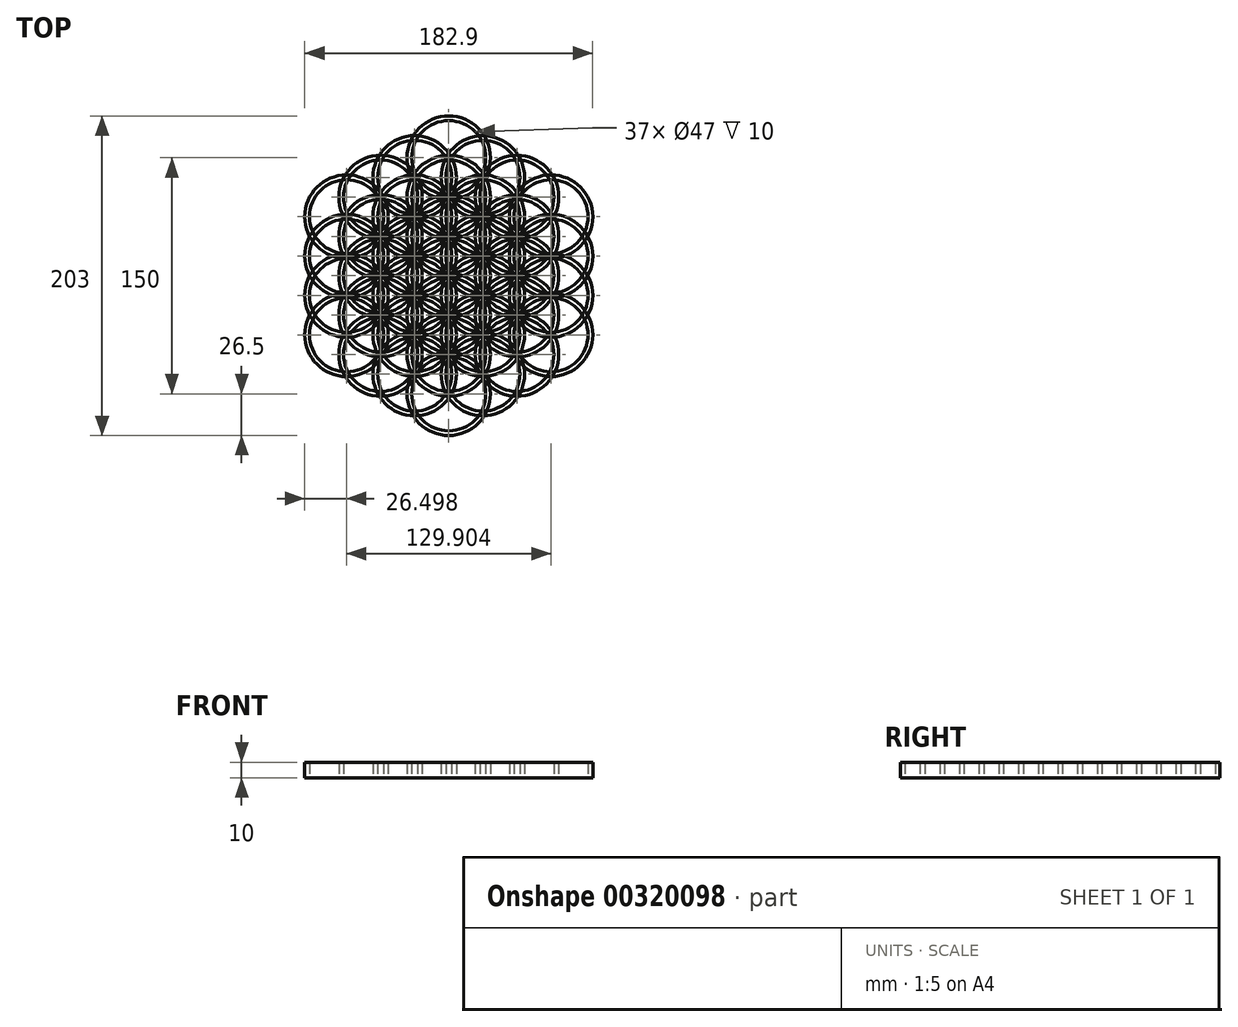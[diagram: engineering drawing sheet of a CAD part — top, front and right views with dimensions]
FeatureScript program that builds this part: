
annotation { "Feature Type Name" : "Feature", "Feature Type Description" : "" }
export const myFeature = defineFeature(function(context is Context, id is Id, definition is map)
    precondition{}
    {
        {
            var Q0;
            Q0=qCreatedBy(makeId("Right.planeOp"),FACE);
            var sketch = newSketch(context, id + "F0", { "sketchPlane" : qUnion([Q0])});
            skLineSegment(sketch, "E0", {"start": v(0, 0) * mm, "end": v(0, -9.37) * mm});
            skSolve(sketch);
        }
        {
            var Q0;
            Q0=qCreatedBy(makeId("Top.planeOp"),FACE);
            var sketch = newSketch(context, id + "F1", { "sketchPlane" : qUnion([Q0])});
            skCircle(sketch, "E1", {"center": v(0, 0) * mm, "radius": 25 * mm, "construction": true});
            skCircle(sketch, "E2.0", {"center": v(0, 0) * mm, "radius": 26.5 * mm});
            skCircle(sketch, "E3.0", {"center": v(0, 0) * mm, "radius": 23.5 * mm});
            skSolve(sketch);
        }
        {
            var Q0;
            Q0=makeQuery(id+"F1.imprint","IMPRINT",FACE,{"disambiguationData":[TD([[makeQuery(id+"F1.imprint","IMPRINT",EDGE,{"derivedFrom":sQuery(id+"F1.wireOp",EDGE,"E2.0")}),1.0]])]});
            extrude(context, id + "F2", {"entities" : qUnion([Q0]), "depth" : 10 * mm});
        }
        {
            var Q0;
            Q0=qCreatedBy(makeId("Top.planeOp"),FACE);
            var sketch = newSketch(context, id + "F3", { "sketchPlane" : qUnion([Q0])});
            skCircle(sketch, "E4", {"center": v(0, 25) * mm, "radius": 25 * mm, "construction": true});
            skCircle(sketch, "E5.0", {"center": v(0, 25) * mm, "radius": 26.5 * mm});
            skCircle(sketch, "E6.0", {"center": v(0, 25) * mm, "radius": 23.5 * mm});
            skCircle(sketch, "E7", {"center": v(0, 0) * mm, "radius": 25 * mm, "construction": true});
            skCircle(sketch, "E8.0", {"center": v(0, 0) * mm, "radius": 26.5 * mm, "construction": true});
            skCircle(sketch, "E9.0", {"center": v(0, 0) * mm, "radius": 23.5 * mm, "construction": true});
            skSolve(sketch);
        }
        {
            var Q0;
            Q0 = qSketchRegion(id + "F3", true);
            extrude(context, id + "F4", {"entities" : qUnion([Q0]), "depth" : 10 * mm});
        }
        {
            var Q0;
            Q0=makeQuery(id+"F4.opExtrude","SWEPT_BODY",BODY,{"disambiguationData":[OSD([sQuery(id+"F3.wireOp",EDGE,"E5.0"),sQuery(id+"F3.wireOp",EDGE,"E6.0")])]});
            var Q1;
            Q1=sQuery(id+"F0.wireOp",EDGE,"E0");
            circularPattern(context, id + "F5", {"entities" : qUnion([Q0]), "axis" : qUnion([Q1]), "angle" : 360 * degree, "instanceCount" : 6, "equalSpace" : true});
        }
        {
            var Q0;
            Q0=qCreatedBy(makeId("Top.planeOp"),FACE);
            var sketch = newSketch(context, id + "F6", { "sketchPlane" : qUnion([Q0])});
            skCircle(sketch, "E10", {"center": v(0, 0) * mm, "radius": 25 * mm, "construction": true});
            skCircle(sketch, "E11.0", {"center": v(0, 0) * mm, "radius": 26.5 * mm, "construction": true});
            skCircle(sketch, "E12.0", {"center": v(0, 0) * mm, "radius": 23.5 * mm, "construction": true});
            skCircle(sketch, "E13", {"center": v(0, 25) * mm, "radius": 25 * mm, "construction": true});
            skCircle(sketch, "E14.0", {"center": v(0, 25) * mm, "radius": 26.5 * mm, "construction": true});
            skCircle(sketch, "E15.0", {"center": v(0, 25) * mm, "radius": 23.5 * mm, "construction": true});
            skCircle(sketch, "E16", {"center": v(-21.65, 12.5) * mm, "radius": 25 * mm, "construction": true});
            skCircle(sketch, "E17.0", {"center": v(-21.65, 12.5) * mm, "radius": 26.5 * mm, "construction": true});
            skCircle(sketch, "E18.0", {"center": v(-21.65, 12.5) * mm, "radius": 23.5 * mm, "construction": true});
            skCircle(sketch, "E19", {"center": v(-21.65, 37.5) * mm, "radius": 25 * mm, "construction": true});
            skCircle(sketch, "E20.0", {"center": v(-21.65, 37.5) * mm, "radius": 26.5 * mm});
            skCircle(sketch, "E21.0", {"center": v(-21.65, 37.5) * mm, "radius": 23.5 * mm});
            skSolve(sketch);
        }
        {
            var Q0;
            Q0=makeQuery(id+"F6.imprint","IMPRINT",FACE,{"disambiguationData":[TD([[makeQuery(id+"F6.imprint","IMPRINT",EDGE,{"derivedFrom":sQuery(id+"F6.wireOp",EDGE,"E20.0")}),1.0]])]});
            extrude(context, id + "F7", {"entities" : qUnion([Q0]), "depth" : 10 * mm});
        }
        {
            var Q0;
            Q0=makeQuery(id+"F7.opExtrude","SWEPT_BODY",BODY,{"disambiguationData":[OSD([sQuery(id+"F6.wireOp",EDGE,"E20.0"),sQuery(id+"F6.wireOp",EDGE,"E21.0")])]});
            var Q1;
            Q1=sQuery(id+"F0.wireOp",EDGE,"E0");
            circularPattern(context, id + "F8", {"entities" : qUnion([Q0]), "axis" : qUnion([Q1]), "angle" : 360 * degree, "instanceCount" : 6, "equalSpace" : true});
        }
        {
            var Q0;
            Q0=qCreatedBy(makeId("Top.planeOp"),FACE);
            var sketch = newSketch(context, id + "F9", { "sketchPlane" : qUnion([Q0])});
            skCircle(sketch, "E22", {"center": v(0, 0) * mm, "radius": 25 * mm, "construction": true});
            skCircle(sketch, "E23.0", {"center": v(0, 0) * mm, "radius": 26.5 * mm, "construction": true});
            skCircle(sketch, "E24.0", {"center": v(0, 0) * mm, "radius": 23.5 * mm, "construction": true});
            skCircle(sketch, "E25", {"center": v(0, 25) * mm, "radius": 25 * mm, "construction": true});
            skCircle(sketch, "E26.0", {"center": v(0, 25) * mm, "radius": 26.5 * mm, "construction": true});
            skCircle(sketch, "E27.0", {"center": v(0, 25) * mm, "radius": 23.5 * mm, "construction": true});
            skCircle(sketch, "E28", {"center": v(-21.65, 12.5) * mm, "radius": 25 * mm, "construction": true});
            skCircle(sketch, "E29.0", {"center": v(-21.65, 12.5) * mm, "radius": 26.5 * mm, "construction": true});
            skCircle(sketch, "E30.0", {"center": v(-21.65, 12.5) * mm, "radius": 23.5 * mm, "construction": true});
            skCircle(sketch, "E31", {"center": v(-21.65, 37.5) * mm, "radius": 25 * mm, "construction": true});
            skCircle(sketch, "E32.0", {"center": v(-21.65, 37.5) * mm, "radius": 26.5 * mm, "construction": true});
            skCircle(sketch, "E33.0", {"center": v(-21.65, 37.5) * mm, "radius": 23.5 * mm, "construction": true});
            skCircle(sketch, "E34", {"center": v(-80.96, 35.25) * mm, "radius": 20 * mm, "construction": true});
            skCircle(sketch, "E35.0", {"center": v(-80.96, 35.25) * mm, "radius": 21.5 * mm, "construction": true});
            skCircle(sketch, "E36.0", {"center": v(-80.96, 35.25) * mm, "radius": 18.5 * mm, "construction": true});
            skCircle(sketch, "E37", {"center": v(-43.3, 25) * mm, "radius": 25 * mm, "construction": true});
            skCircle(sketch, "E38.0", {"center": v(-43.3, 25) * mm, "radius": 26.5 * mm});
            skCircle(sketch, "E39.0", {"center": v(-43.3, 25) * mm, "radius": 23.5 * mm});
            skSolve(sketch);
        }
        {
            var Q0;
            Q0=makeQuery(id+"F9.imprint","IMPRINT",FACE,{"disambiguationData":[TD([[makeQuery(id+"F9.imprint","IMPRINT",EDGE,{"derivedFrom":sQuery(id+"F9.wireOp",EDGE,"E38.0")}),1.0]])]});
            extrude(context, id + "F10", {"entities" : qUnion([Q0]), "depth" : 10 * mm});
        }
        {
            var Q0;
            Q0=makeQuery(id+"F10.opExtrude","SWEPT_BODY",BODY,{"disambiguationData":[OSD([sQuery(id+"F9.wireOp",EDGE,"E38.0"),sQuery(id+"F9.wireOp",EDGE,"E39.0")])]});
            var Q1;
            Q1=sQuery(id+"F0.wireOp",EDGE,"E0");
            circularPattern(context, id + "F11", {"entities" : qUnion([Q0]), "axis" : qUnion([Q1]), "angle" : 360 * degree, "instanceCount" : 6, "equalSpace" : true});
        }
        {
            var Q0;
            Q0=qCreatedBy(makeId("Top.planeOp"),FACE);
            var sketch = newSketch(context, id + "F12", { "sketchPlane" : qUnion([Q0])});
            skCircle(sketch, "E40", {"center": v(0, 0) * mm, "radius": 25 * mm, "construction": true});
            skCircle(sketch, "E41.0", {"center": v(0, 0) * mm, "radius": 26.5 * mm, "construction": true});
            skCircle(sketch, "E42.0", {"center": v(0, 0) * mm, "radius": 23.5 * mm, "construction": true});
            skCircle(sketch, "E43", {"center": v(0, 25) * mm, "radius": 25 * mm, "construction": true});
            skCircle(sketch, "E44.0", {"center": v(0, 25) * mm, "radius": 26.5 * mm, "construction": true});
            skCircle(sketch, "E45.0", {"center": v(0, 25) * mm, "radius": 23.5 * mm, "construction": true});
            skCircle(sketch, "E46", {"center": v(-21.65, 12.5) * mm, "radius": 25 * mm, "construction": true});
            skCircle(sketch, "E47.0", {"center": v(-21.65, 12.5) * mm, "radius": 26.5 * mm, "construction": true});
            skCircle(sketch, "E48.0", {"center": v(-21.65, 12.5) * mm, "radius": 23.5 * mm, "construction": true});
            skCircle(sketch, "E49", {"center": v(-21.65, 37.5) * mm, "radius": 25 * mm, "construction": true});
            skCircle(sketch, "E50.0", {"center": v(-21.65, 37.5) * mm, "radius": 26.5 * mm, "construction": true});
            skCircle(sketch, "E51.0", {"center": v(-21.65, 37.5) * mm, "radius": 23.5 * mm, "construction": true});
            skCircle(sketch, "E52", {"center": v(-43.3, 50) * mm, "radius": 25 * mm, "construction": true});
            skCircle(sketch, "E53.0", {"center": v(-43.3, 50) * mm, "radius": 26.5 * mm});
            skCircle(sketch, "E54.0", {"center": v(-43.3, 50) * mm, "radius": 23.5 * mm});
            skCircle(sketch, "E55", {"center": v(-43.3, 25) * mm, "radius": 25 * mm, "construction": true});
            skCircle(sketch, "E56.0", {"center": v(-43.3, 25) * mm, "radius": 26.5 * mm, "construction": true});
            skCircle(sketch, "E57.0", {"center": v(-43.3, 25) * mm, "radius": 23.5 * mm, "construction": true});
            skSolve(sketch);
        }
        {
            var Q0;
            Q0=makeQuery(id+"F12.imprint","IMPRINT",FACE,{"disambiguationData":[TD([[makeQuery(id+"F12.imprint","IMPRINT",EDGE,{"derivedFrom":sQuery(id+"F12.wireOp",EDGE,"E53.0")}),1.0]])]});
            extrude(context, id + "F13", {"entities" : qUnion([Q0]), "depth" : 10 * mm});
        }
        {
            var Q0;
            Q0=makeQuery(id+"F13.opExtrude","SWEPT_BODY",BODY,{"disambiguationData":[OSD([sQuery(id+"F12.wireOp",EDGE,"E53.0"),sQuery(id+"F12.wireOp",EDGE,"E54.0")])]});
            var Q1;
            Q1=sQuery(id+"F0.wireOp",EDGE,"E0");
            circularPattern(context, id + "F14", {"entities" : qUnion([Q0]), "axis" : qUnion([Q1]), "angle" : 360 * degree, "instanceCount" : 6, "equalSpace" : true});
        }
        {
            var Q0;
            Q0=qCreatedBy(makeId("Top.planeOp"),FACE);
            var sketch = newSketch(context, id + "F15", { "sketchPlane" : qUnion([Q0])});
            skCircle(sketch, "E58", {"center": v(0, 0) * mm, "radius": 25 * mm, "construction": true});
            skCircle(sketch, "E59.0", {"center": v(0, 0) * mm, "radius": 26.5 * mm, "construction": true});
            skCircle(sketch, "E60.0", {"center": v(0, 0) * mm, "radius": 23.5 * mm, "construction": true});
            skCircle(sketch, "E61", {"center": v(0, 25) * mm, "radius": 25 * mm, "construction": true});
            skCircle(sketch, "E62.0", {"center": v(0, 25) * mm, "radius": 26.5 * mm, "construction": true});
            skCircle(sketch, "E63.0", {"center": v(0, 25) * mm, "radius": 23.5 * mm, "construction": true});
            skCircle(sketch, "E64", {"center": v(-21.65, 12.5) * mm, "radius": 25 * mm, "construction": true});
            skCircle(sketch, "E65.0", {"center": v(-21.65, 12.5) * mm, "radius": 26.5 * mm, "construction": true});
            skCircle(sketch, "E66.0", {"center": v(-21.65, 12.5) * mm, "radius": 23.5 * mm, "construction": true});
            skCircle(sketch, "E67", {"center": v(-21.65, 37.5) * mm, "radius": 25 * mm, "construction": true});
            skCircle(sketch, "E68.0", {"center": v(-21.65, 37.5) * mm, "radius": 26.5 * mm, "construction": true});
            skCircle(sketch, "E69.0", {"center": v(-21.65, 37.5) * mm, "radius": 23.5 * mm, "construction": true});
            skCircle(sketch, "E70", {"center": v(-43.3, 50) * mm, "radius": 25 * mm, "construction": true});
            skCircle(sketch, "E71.0", {"center": v(-43.3, 50) * mm, "radius": 26.5 * mm, "construction": true});
            skCircle(sketch, "E72.0", {"center": v(-43.3, 50) * mm, "radius": 23.5 * mm, "construction": true});
            skCircle(sketch, "E73", {"center": v(-43.3, 25) * mm, "radius": 25 * mm, "construction": true});
            skCircle(sketch, "E74.0", {"center": v(-43.3, 25) * mm, "radius": 26.5 * mm, "construction": true});
            skCircle(sketch, "E75.0", {"center": v(-43.3, 25) * mm, "radius": 23.5 * mm, "construction": true});
            skCircle(sketch, "E76", {"center": v(-21.65, 62.5) * mm, "radius": 25 * mm, "construction": true});
            skCircle(sketch, "E77.0", {"center": v(-21.65, 62.5) * mm, "radius": 26.5 * mm});
            skCircle(sketch, "E78.0", {"center": v(-21.65, 62.5) * mm, "radius": 23.5 * mm});
            skSolve(sketch);
        }
        {
            var Q0;
            Q0=makeQuery(id+"F15.imprint","IMPRINT",FACE,{"disambiguationData":[TD([[makeQuery(id+"F15.imprint","IMPRINT",EDGE,{"derivedFrom":sQuery(id+"F15.wireOp",EDGE,"E77.0")}),1.0]])]});
            extrude(context, id + "F16", {"entities" : qUnion([Q0]), "depth" : 10 * mm});
        }
        {
            var Q0;
            Q0=makeQuery(id+"F16.opExtrude","SWEPT_BODY",BODY,{"disambiguationData":[OSD([sQuery(id+"F15.wireOp",EDGE,"E77.0"),sQuery(id+"F15.wireOp",EDGE,"E78.0")])]});
            var Q1;
            Q1=sQuery(id+"F0.wireOp",EDGE,"E0");
            circularPattern(context, id + "F17", {"entities" : qUnion([Q0]), "axis" : qUnion([Q1]), "angle" : 360 * degree, "instanceCount" : 6, "equalSpace" : true});
        }
        {
            var Q0;
            Q0=qCreatedBy(makeId("Top.planeOp"),FACE);
            var sketch = newSketch(context, id + "F18", { "sketchPlane" : qUnion([Q0])});
            skCircle(sketch, "E79", {"center": v(0, 0) * mm, "radius": 25 * mm, "construction": true});
            skCircle(sketch, "E80.0", {"center": v(0, 0) * mm, "radius": 26.5 * mm, "construction": true});
            skCircle(sketch, "E81.0", {"center": v(0, 0) * mm, "radius": 23.5 * mm, "construction": true});
            skCircle(sketch, "E82", {"center": v(0, 25) * mm, "radius": 25 * mm, "construction": true});
            skCircle(sketch, "E83.0", {"center": v(0, 25) * mm, "radius": 26.5 * mm, "construction": true});
            skCircle(sketch, "E84.0", {"center": v(0, 25) * mm, "radius": 23.5 * mm, "construction": true});
            skCircle(sketch, "E85", {"center": v(-21.65, 12.5) * mm, "radius": 25 * mm, "construction": true});
            skCircle(sketch, "E86.0", {"center": v(-21.65, 12.5) * mm, "radius": 26.5 * mm, "construction": true});
            skCircle(sketch, "E87.0", {"center": v(-21.65, 12.5) * mm, "radius": 23.5 * mm, "construction": true});
            skCircle(sketch, "E88", {"center": v(-21.65, 37.5) * mm, "radius": 25 * mm, "construction": true});
            skCircle(sketch, "E89.0", {"center": v(-21.65, 37.5) * mm, "radius": 26.5 * mm, "construction": true});
            skCircle(sketch, "E90.0", {"center": v(-21.65, 37.5) * mm, "radius": 23.5 * mm, "construction": true});
            skCircle(sketch, "E91", {"center": v(-43.3, 50) * mm, "radius": 25 * mm, "construction": true});
            skCircle(sketch, "E92.0", {"center": v(-43.3, 50) * mm, "radius": 26.5 * mm, "construction": true});
            skCircle(sketch, "E93.0", {"center": v(-43.3, 50) * mm, "radius": 23.5 * mm, "construction": true});
            skCircle(sketch, "E94", {"center": v(-43.3, 25) * mm, "radius": 25 * mm, "construction": true});
            skCircle(sketch, "E95.0", {"center": v(-43.3, 25) * mm, "radius": 26.5 * mm, "construction": true});
            skCircle(sketch, "E96.0", {"center": v(-43.3, 25) * mm, "radius": 23.5 * mm, "construction": true});
            skCircle(sketch, "E97", {"center": v(-21.65, 62.5) * mm, "radius": 25 * mm, "construction": true});
            skCircle(sketch, "E98.0", {"center": v(-21.65, 62.5) * mm, "radius": 26.5 * mm, "construction": true});
            skCircle(sketch, "E99.0", {"center": v(-21.65, 62.5) * mm, "radius": 23.5 * mm, "construction": true});
            skCircle(sketch, "E100", {"center": v(0, 75) * mm, "radius": 25 * mm, "construction": true});
            skCircle(sketch, "E101.0", {"center": v(0, 75) * mm, "radius": 26.5 * mm});
            skCircle(sketch, "E102.0", {"center": v(0, 75) * mm, "radius": 23.5 * mm});
            skSolve(sketch);
        }
        {
            var Q0;
            Q0=makeQuery(id+"F18.imprint","IMPRINT",FACE,{"disambiguationData":[TD([[makeQuery(id+"F18.imprint","IMPRINT",EDGE,{"derivedFrom":sQuery(id+"F18.wireOp",EDGE,"E101.0")}),1.0]])]});
            extrude(context, id + "F19", {"entities" : qUnion([Q0]), "depth" : 10 * mm});
        }
        {
            var Q0;
            Q0=makeQuery(id+"F19.opExtrude","SWEPT_BODY",BODY,{"disambiguationData":[OSD([sQuery(id+"F18.wireOp",EDGE,"E101.0"),sQuery(id+"F18.wireOp",EDGE,"E102.0")])]});
            var Q1;
            Q1=sQuery(id+"F0.wireOp",EDGE,"E0");
            circularPattern(context, id + "F20", {"entities" : qUnion([Q0]), "axis" : qUnion([Q1]), "angle" : 360 * degree, "instanceCount" : 6, "equalSpace" : true});
        }
    });
